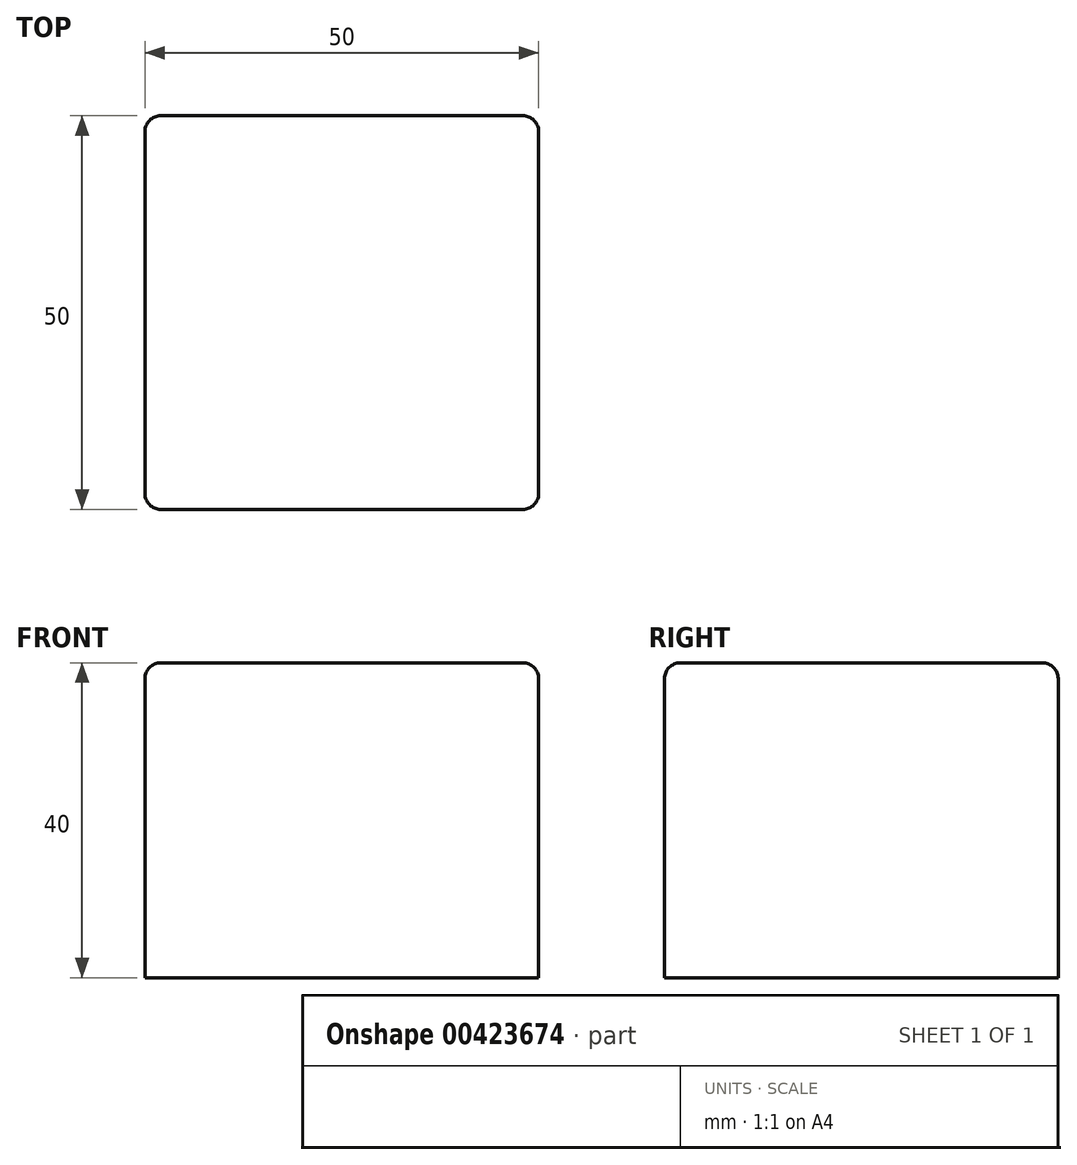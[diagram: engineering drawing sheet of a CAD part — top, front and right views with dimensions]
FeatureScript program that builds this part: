
annotation { "Feature Type Name" : "Feature", "Feature Type Description" : "" }
export const myFeature = defineFeature(function(context is Context, id is Id, definition is map)
    precondition{}
    {
        {
            var Q0;
            Q0=qCreatedBy(makeId("Top.planeOp"),FACE);
            var sketch = newSketch(context, id + "F0", { "sketchPlane" : qUnion([Q0])});
            skLineSegment(sketch, "E0.bottom", {"start": v(25, 25) * mm, "end": v(-25, 25) * mm});
            skLineSegment(sketch, "E0.top", {"start": v(25, -25) * mm, "end": v(-25, -25) * mm});
            skLineSegment(sketch, "E0.left", {"start": v(25, 25) * mm, "end": v(25, -25) * mm});
            skLineSegment(sketch, "E0.right", {"start": v(-25, 25) * mm, "end": v(-25, -25) * mm});
            skPoint(sketch, "E0.middle", {"position": v(0, 0) * mm});
            skSolve(sketch);
        }
        {
            var Q0;
            Q0=makeQuery(id+"F0.imprint","IMPRINT",FACE,{"disambiguationData":[TD([[makeQuery(id+"F0.imprint","IMPRINT",EDGE,{"derivedFrom":sQuery(id+"F0.wireOp",EDGE,"E0.bottom")}),1.0]])]});
            extrude(context, id + "F1", {"entities" : qUnion([Q0]), "depth" : 40 * mm});
        }
        {
            var Q0;
            Q0=makeQuery(id+"F1.opExtrude","SWEPT_EDGE",EDGE,{"disambiguationData":[OSD([sQuery(id+"F0.wireOp",EDGE,"E0.top"),sQuery(id+"F0.wireOp",EDGE,"E0.left")])]});
            var Q1;
            Q1=makeQuery(id+"F1.opExtrude","SWEPT_EDGE",EDGE,{"disambiguationData":[OSD([sQuery(id+"F0.wireOp",EDGE,"E0.top"),sQuery(id+"F0.wireOp",EDGE,"E0.right")])]});
            var Q2;
            Q2=makeQuery(id+"F1.opExtrude","CAP_EDGE",EDGE,{"disambiguationData":[OSD([sQuery(id+"F0.wireOp",EDGE,"E0.top")])],"isStart":false});
            var Q3;
            Q3=makeQuery(id+"F1.opExtrude","CAP_EDGE",EDGE,{"disambiguationData":[OSD([sQuery(id+"F0.wireOp",EDGE,"E0.left")])],"isStart":false});
            var Q4;
            Q4=makeQuery(id+"F1.opExtrude","SWEPT_EDGE",EDGE,{"disambiguationData":[OSD([sQuery(id+"F0.wireOp",EDGE,"E0.bottom"),sQuery(id+"F0.wireOp",EDGE,"E0.left")])]});
            var Q5;
            Q5=makeQuery(id+"F1.opExtrude","CAP_EDGE",EDGE,{"disambiguationData":[OSD([sQuery(id+"F0.wireOp",EDGE,"E0.bottom")])],"isStart":false});
            var Q6;
            Q6=makeQuery(id+"F1.opExtrude","SWEPT_EDGE",EDGE,{"disambiguationData":[OSD([sQuery(id+"F0.wireOp",EDGE,"E0.bottom"),sQuery(id+"F0.wireOp",EDGE,"E0.right")])]});
            var Q7;
            Q7=makeQuery(id+"F1.opExtrude","CAP_EDGE",EDGE,{"disambiguationData":[OSD([sQuery(id+"F0.wireOp",EDGE,"E0.right")])],"isStart":false});
            fillet(context, id + "F2", {"entities" : qUnion([Q0, Q1, Q2, Q3, Q4, Q5, Q6, Q7]), "radius" : 2 * mm, "tangentPropagation" : true, "allowEdgeOverflow" : false});
        }
    });
